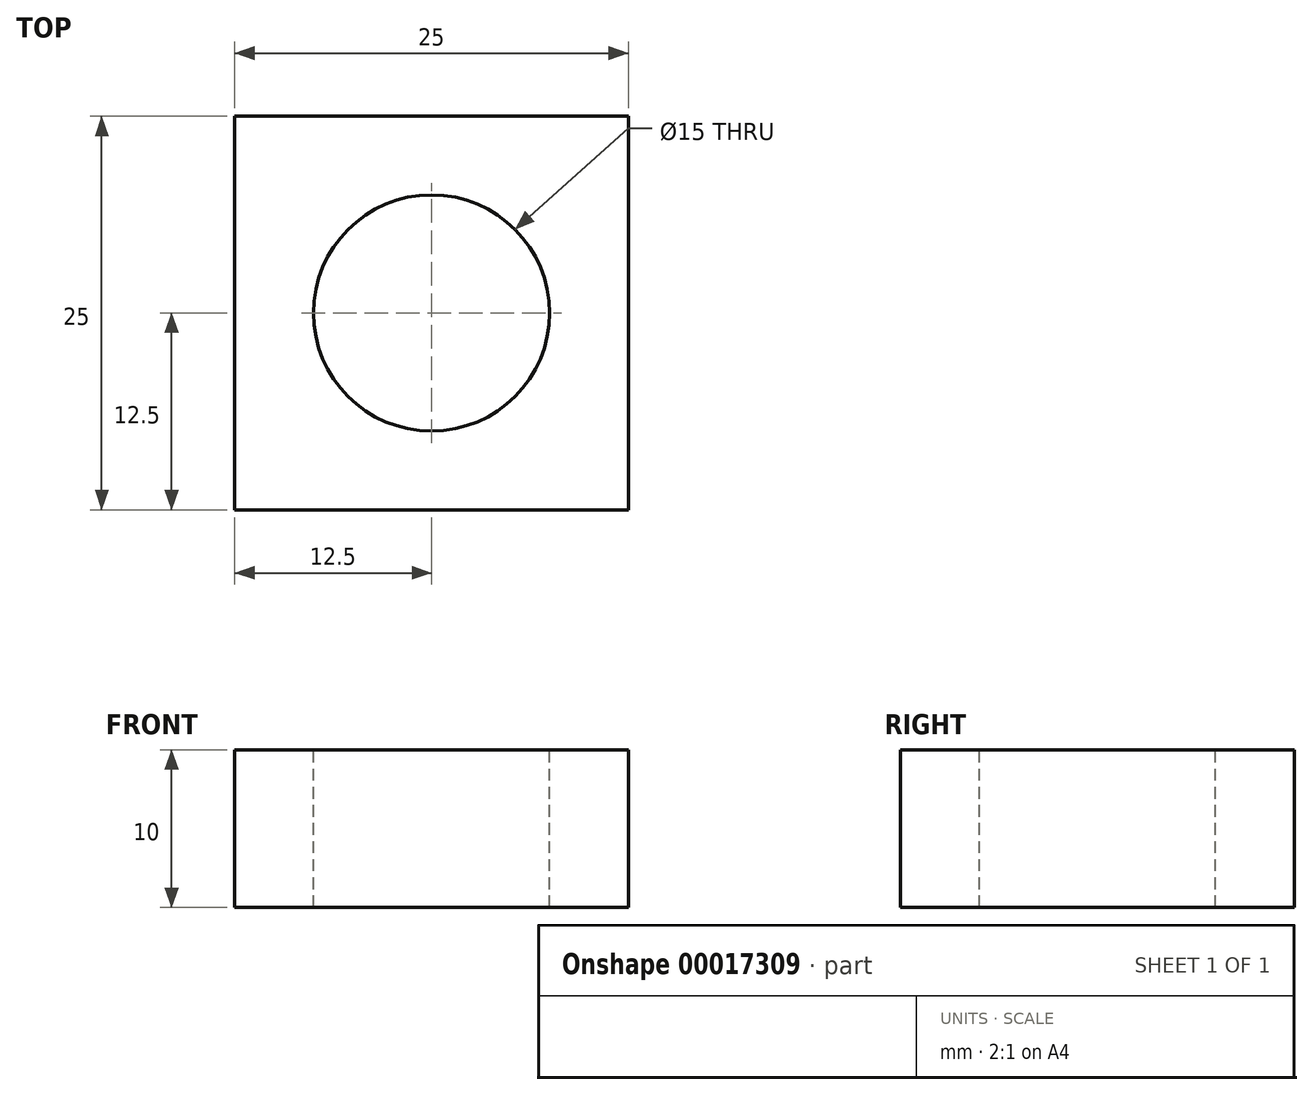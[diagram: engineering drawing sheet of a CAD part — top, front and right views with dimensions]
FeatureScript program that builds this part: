
annotation { "Feature Type Name" : "Feature", "Feature Type Description" : "" }
export const myFeature = defineFeature(function(context is Context, id is Id, definition is map)
    precondition{}
    {
        {
            var Q0;
            Q0=qCreatedBy(makeId("Front.planeOp"),FACE);
            var sketch = newSketch(context, id + "F0", { "sketchPlane" : qUnion([Q0])});
            skLineSegment(sketch, "E0.bottom", {"start": v(0, 0) * mm, "end": v(-25, 0) * mm});
            skLineSegment(sketch, "E0.top", {"start": v(0, 10) * mm, "end": v(-25, 10) * mm});
            skLineSegment(sketch, "E0.left", {"start": v(0, 0) * mm, "end": v(0, 10) * mm});
            skLineSegment(sketch, "E0.right", {"start": v(-25, 0) * mm, "end": v(-25, 10) * mm});
            skSolve(sketch);
        }
        {
            var Q0;
            Q0=makeQuery(id+"F0.imprint","IMPRINT",FACE,{"disambiguationData":[TD([[makeQuery(id+"F0.imprint","IMPRINT",EDGE,{"derivedFrom":sQuery(id+"F0.wireOp",EDGE,"E0.bottom")}),-1.0]])]});
            extrude(context, id + "F1", {"entities" : qUnion([Q0]), "depth" : 25 * mm});
        }
        {
            var Q0;
            Q0=makeQuery(id+"F1.opExtrude","SWEPT_FACE",FACE,{"disambiguationData":[OSD([sQuery(id+"F0.wireOp",EDGE,"E0.top")])]});
            var sketch = newSketch(context, id + "F2", { "sketchPlane" : qUnion([Q0])});
            skCircle(sketch, "E1", {"center": v(-12.5, -12.5) * mm, "radius": 7.5 * mm});
            skPoint(sketch, "E2.trimOffspring.end.orphan", {"position": v(0, -25) * mm});
            skPoint(sketch, "E3.start.orphan", {"position": v(-25, 0) * mm});
            skSolve(sketch);
        }
        {
            var Q0;
            Q0=makeQuery(id+"F2.imprint","IMPRINT",FACE,{"disambiguationData":[TD([[makeQuery(id+"F2.imprint","IMPRINT",EDGE,{"derivedFrom":sQuery(id+"F2.wireOp",EDGE,"E1")}),1.0]])]});
            extrude(context, id + "F3", {"entities" : qUnion([Q0]), "operationType" : NewBodyOperationType.REMOVE, "oppositeDirection" : true, "depth" : 25 * mm});
        }
    });
